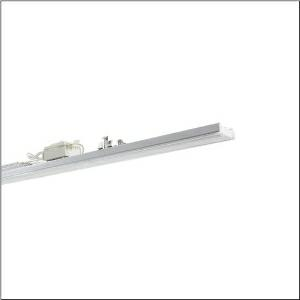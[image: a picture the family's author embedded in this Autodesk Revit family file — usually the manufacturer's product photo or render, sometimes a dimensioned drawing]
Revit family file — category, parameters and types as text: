
# Revit family: licross_r__21_recessed_ho_52tl12dn4fxm_8daa
name_source: partatom
category: Lighting Fixtures
units: mm (PartAtom-declared; Revit-internal decimal feet)

## family parameters
Cut with Voids When Loaded = No
Host = Face
Light Source = No
Part Type = Normal
Room Calculation Point = No
Round Connector Dimension = Use Diameter
Shared = No

## types (1)
- --- (1 x LED, 15000 lm, 84.6 W, 4000K)
    Apparent Load = 85 VA
    CIE Flux Codes = 69 91 98 100 100
    Color Rendering = 80
    Color Temperature = 4000K
    Default Elevation = 1800 mm
    Description = Licross® 21 Recessed HO, luminaire insert, of sheet steel, galvanised, coil coated, white, length: 1.500mm, width: 66mm, height: 67mm, LED rated luminous flux: 15.000lm, light colour: 840, control gear: DALI 2, with plug, 5-pole, with phase selection, mains connection: 220..240V, AC, 50/60Hz, rated input power: 85W, halogen-free wiring, primary optical cover: cover, of PMMA, light emission: direct distribution, primary light characteristic: symmetric, protection rating (complete): IP40, insulation class (complete): insulation class I (protective earthing), certification: CE, ENEC, VDE, UKCA, protection symbol: D if used in an environment without relevant dust loads with corresponding accessories, impact resistance: IK06, permissible ambient temperature for indoor applications: -25..+30°C, corresponds to IFS (International Featured Standards) requirements for safety and quality in the food industry, reducing of maximum allowable ambient temperature of 5°C with ceiling mounting, LABS conformity tested according to VDMA 24364:2018-05, packaging unit: 1 piece
    Height = 58 mm
    Lamp = 1 x LED
    Lamp Light Flux = 15000 lm
    Lamp Power = 84.6 W
    Lamp count = 1
    Length = 1500 mm
    Luminous efficacy = 177 lm/W
    Manufacturer = Siteco
    ModVariant = No
    Model = 52TL12DN4FXM
    Mounting Place = Ceiling
    Mounting Type = Pendant
    Number of Poles = 1
    OnlyDefault = Yes
    Power Factor = 1
    Product Name = Licross® 21 Recessed HO
    Product group = luminaire insert
    ProductGroupID = 902
    Protection Class = Protection class I
    Protection Degree = IP 40
    RLX_Detail_Level = 1
    RLX_Emergency_Light_Flux = 0 lm
    RLX_Emergency_Type = 0
    RLX_Emergency_Type_DB = No
    RlxData = <blob elided: 24593 chars, md5=730a88b8>
    Socket = socket
    Standby Power = 0 W
    System Light Flux = 15000 lm
    System Power = 85 W
    Type Comments = factory setting: luminous flux: 100 % | dim-lin: 254 | 484 mA
    Type Image = l_1296930.jpg
    URL = http://relux.com
    VarID = @adj_116558
    Voltage = 0 V
    Weight = 0.00 kg
    Width = 66 mm

## geometry (parser evidence)
native form markers: Blend x4, Sweep x13
no freeform markers — native parametric forms only
